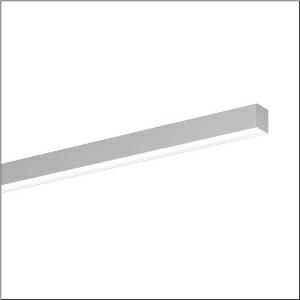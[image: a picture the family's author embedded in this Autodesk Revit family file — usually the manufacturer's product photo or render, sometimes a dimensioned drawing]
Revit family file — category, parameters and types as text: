
# Revit family: silica_r__21_51mx23da34sb_798d
name_source: partatom
category: Lighting Fixtures
units: mm (PartAtom-declared; Revit-internal decimal feet)

## family parameters
Cut with Voids When Loaded = No
Host = Face
Light Source = No
Part Type = Normal
Room Calculation Point = No
Round Connector Dimension = Use Diameter
Shared = No

## types (1)
- --- (1 x LED, 3280 lm, 24.1 W, 3000K)
    Apparent Load = 24 VA
    CIE Flux Codes = 78 96 99 100 100
    Color Rendering = 80
    Color Temperature = 3000K
    Default Elevation = 1800 mm
    Description = Silica® 21, office luminaire, primary optical cover: prismatic diffuser, of PMMA, CAT 2 (L<= 3000cd/m²), light emission: direct distribution, primary light characteristic: symmetric, installation type: surface-mounted, LED, rated luminous flux: 3.280lm, luminous efficacy: 136lm/W, light colour: 830, colour temperature: 3000K, control gear: DALI 2, with terminal, 3+2-pole, max. 2.5mm², mains connection: 220..240V, AC, 50/60Hz, rated input power: 24.1W, luminaire housing, of aluminium, metallic grey (RAL 9006), length: 1.204mm, width: 53mm, height: 53mm, protection rating (complete): IP20, insulation class (complete): insulation class I (protective earthing), certification: CE, permissible operating ambient temperature: 0..+35°C, standard: EN 50419, packaging unit: 1 piece
    Height = 53 mm
    Lamp = 1 x LED
    Lamp Light Flux = 3280 lm
    Lamp Power = 24.1 W
    Lamp count = 1
    Length = 1204 mm
    Luminous efficacy = 136 lm/W
    Manufacturer = Siteco
    ModVariant = No
    Model = 51MX23DA34SB
    Mounting Place = Ceiling
    Mounting Type = Surface mounted
    Number of Poles = 1
    OnlyDefault = Yes
    Power Factor = 1
    Product Name = Silica® 21
    Product group = office luminaire | ceiling mounted
    ProductGroupID = 302
    Protection Class = Protection class I
    Protection Degree = IP 20
    RLX_Detail_Level = 1
    RLX_Emergency_Light_Flux = 0 lm
    RLX_Emergency_Type = 0
    RLX_Emergency_Type_DB = No
    RlxData = <blob elided: 21297 chars, md5=f8385734>
    Socket = socket
    Standby Power = 0 W
    System Light Flux = 3280 lm
    System Power = 24 W
    Type Comments = factory setting: luminous flux: 100 % | dim-lin: 254 | 345 mA
    Type Image = l_1335933.jpg
    URL = http://relux.com
    VarID = @adj_007827
    Voltage = 0 V
    Weight = 0.00 kg
    Width = 53 mm

## geometry (parser evidence)
native form markers: Blend x4, Sweep x11
no freeform markers — native parametric forms only
